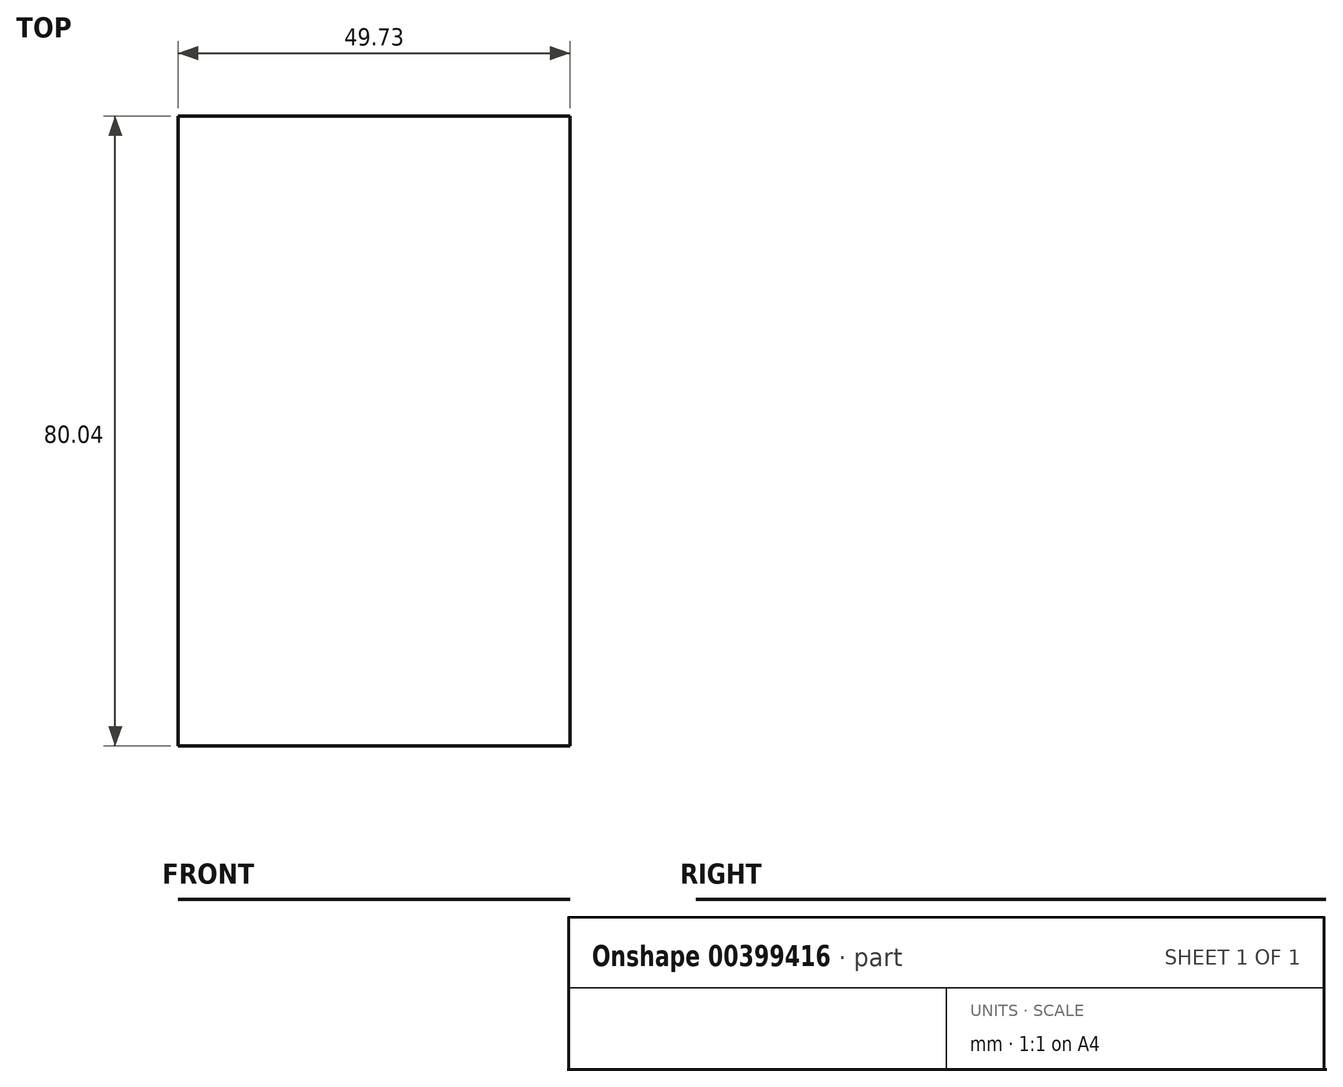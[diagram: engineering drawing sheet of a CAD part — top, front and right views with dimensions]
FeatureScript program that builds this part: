
annotation { "Feature Type Name" : "Feature", "Feature Type Description" : "" }
export const myFeature = defineFeature(function(context is Context, id is Id, definition is map)
    precondition{}
    {
        {
            var Q0;
            Q0=qCreatedBy(makeId("Front.planeOp"),FACE);
            var sketch = newSketch(context, id + "F0", { "sketchPlane" : qUnion([Q0])});
            skLineSegment(sketch, "E0.bottom", {"start": v(49.73, 62.27) * mm, "end": v(0, 62.27) * mm});
            skLineSegment(sketch, "E0.top", {"start": v(49.73, 0) * mm, "end": v(0, 0) * mm});
            skLineSegment(sketch, "E0.left", {"start": v(49.73, 62.27) * mm, "end": v(49.73, 0) * mm});
            skLineSegment(sketch, "E0.right", {"start": v(0, 62.27) * mm, "end": v(0, 0) * mm});
            skSolve(sketch);
        }
        {
            var Q0;
            Q0 = qSketchRegion(id + "F0", true);
            var Q1;
            Q1=sQuery(id+"F0.wireOp",EDGE,"E0.bottom");
            extrude(context, id + "F1", {"entities" : qUnion([Q0]), "bodyType" : ToolBodyType.SURFACE, "surfaceEntities" : qUnion([Q1]), "depth" : 80.04 * mm});
        }
    });
